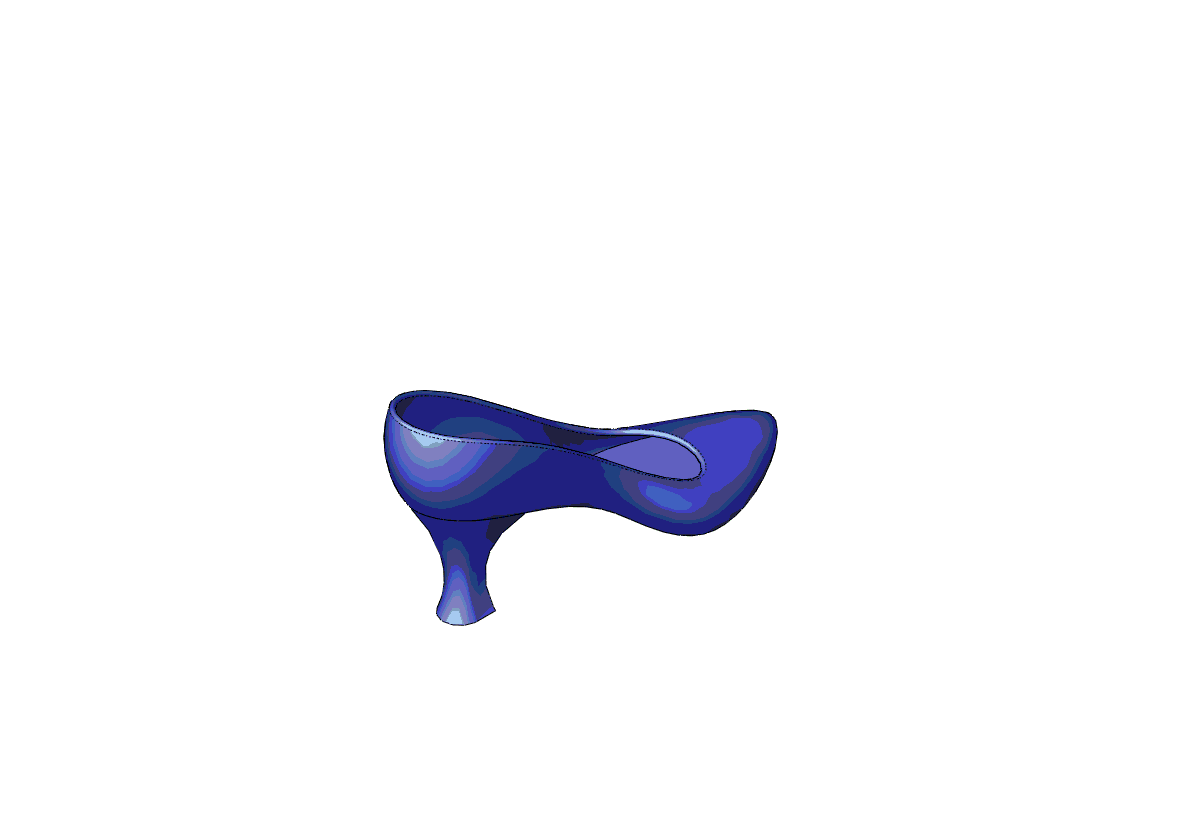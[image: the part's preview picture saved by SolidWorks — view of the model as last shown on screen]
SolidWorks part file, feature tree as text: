
SOLIDWORKS PART (.sldprt)
format: sldprt  version: not decoded by parser v0  size: 331,264 bytes
history: native  units: mm
features: sketch x10, plane x8, surface_op x2, material x1, fillet x1 (+11 scaffold rows collapsed)
feature tree (33):
  scaffold x11  (default folders/planes/origin — collapsed)
  material  "Material <not specified>"
  plane  "Front XY"
  plane  "Top XZ"
  plane  "Right YZ"
  sketch  "Sketch1"
  plane  "Plane1"
  plane  "Plane2"
  plane  "Plane3"
  sketch  "Sketch2"
  sketch  "Sketch3"
  sketch  "Sketch4"  dims[D1=~7.590901mm]
  sketch  "Sketch5"  dims[D1=~12.793796mm D2=~8.153617mm D3=~17.24515mm]
  plane  "Plane4"
  sketch  "Sketch6"
  surface_op  "Surface-Extrude1"
  sketch  "Sketch7"
  surface_op  "Surface-Trim2"
  sketch  "Sketch8"
  plane  "Plane5"  Offset=4.809733mm
  sketch  "Sketch9"  dims[D1=0.508mm]
  sketch  "Sketch10"  dims[D1=0.508mm]
  fillet  "Fillet1"  Radius=45.183511mm thickness=45.183511mm
decode coverage: 5 of 13 modeling features carry decoded parameters
note: ~ marks probable driven/reference dimensions
note: suppression state not decoded; provenance and decode notes live in map.json
